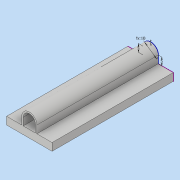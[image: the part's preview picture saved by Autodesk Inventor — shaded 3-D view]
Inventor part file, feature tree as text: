
AUTODESK INVENTOR PART (.ipt)
format: ipt  version: 2019 (Build 230136000, 136)  size: 138,752 bytes
history: native  units: mm
features: extrude x4, sketch x3
ambient origin geometry x8: Origin, YZ Plane, XZ Plane, XY Plane, X Axis, Y Axis, Z Axis, Center Point
bodies: Body1 (feature_tree)
feature tree (7):
  extrude  "Выдавливание9"  Depth=10.0mm
  sketch  "Эскиз8"
  extrude  "Выдавливание14"  Depth=5.0mm
  extrude  "Выдавливание15"  Depth=5.0mm
  extrude  "Выдавливание16"  Depth=80.0mm TaperAngle=0.0deg
  sketch  "Эскиз9"
  sketch  "Эскиз10"
